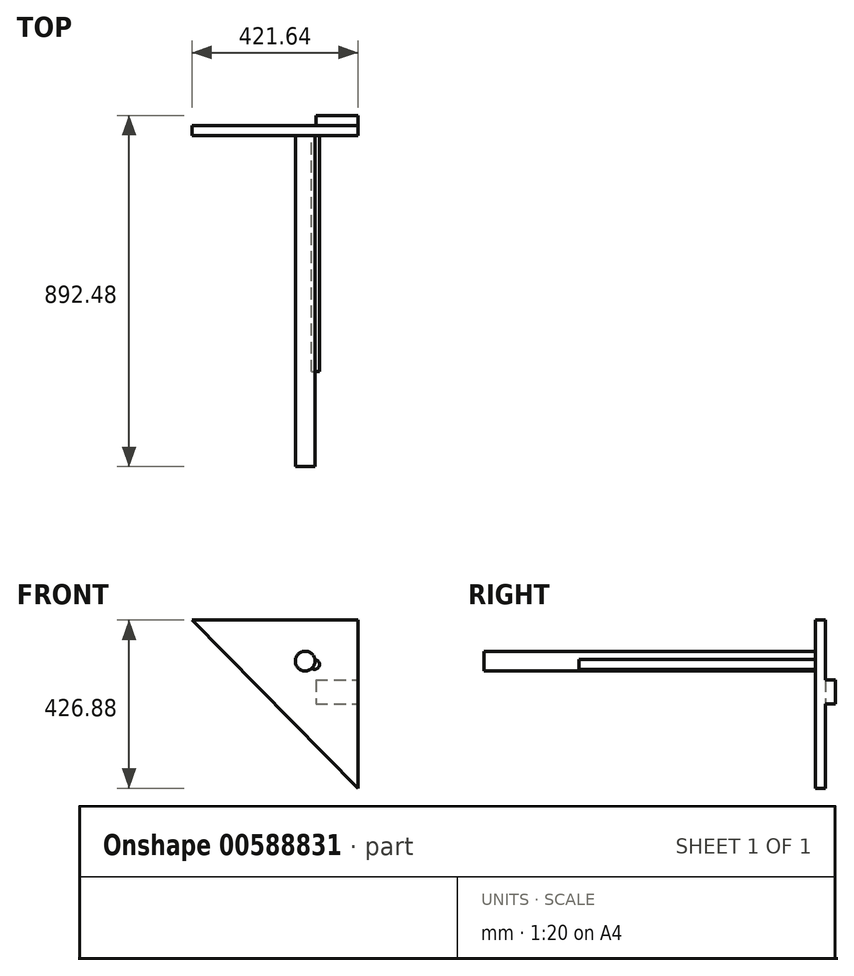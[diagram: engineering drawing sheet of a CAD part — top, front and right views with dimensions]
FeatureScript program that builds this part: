
annotation { "Feature Type Name" : "Feature", "Feature Type Description" : "" }
export const myFeature = defineFeature(function(context is Context, id is Id, definition is map)
    precondition{}
    {
        {
            var Q0;
            Q0=qCreatedBy(makeId("Front.planeOp"),FACE);
            var sketch = newSketch(context, id + "F0", { "sketchPlane" : qUnion([Q0])});
            skLineSegment(sketch, "E0", {"start": v(-421.64, 0) * mm, "end": v(0, 0) * mm});
            skLineSegment(sketch, "E1", {"start": v(0, 0) * mm, "end": v(0, -426.88) * mm});
            skLineSegment(sketch, "E2", {"start": v(0, -426.88) * mm, "end": v(-421.64, 0) * mm});
            skSolve(sketch);
        }
        {
            var Q0;
            Q0 = qSketchRegion(id + "F0", true);
            extrude(context, id + "F1", {"entities" : qUnion([Q0]), "depth" : 25.4 * mm, "offsetDistance" : 25.4 * mm});
        }
        {
            var Q0;
            Q0=makeQuery(id+"F1.opExtrude","CAP_FACE",FACE,{"disambiguationData":[OSD([sQuery(id+"F0.wireOp",EDGE,"E0"),sQuery(id+"F0.wireOp",EDGE,"E1"),sQuery(id+"F0.wireOp",EDGE,"E2")])],"isStart":false});
            var sketch = newSketch(context, id + "F2", { "sketchPlane" : qUnion([Q0])});
            skCircle(sketch, "E3", {"center": v(-110.56, -112.6) * mm, "radius": 12.5 * mm});
            skSolve(sketch);
        }
        {
            var Q0;
            Q0 = qSketchRegion(id + "F2", true);
            extrude(context, id + "F3", {"entities" : qUnion([Q0]), "operationType" : NewBodyOperationType.ADD, "endBound" : BoundingType.THROUGH_ALL, "depth" : 25.4 * mm, "offsetDistance" : 25.4 * mm});
        }
        {
            var Q0;
            Q0=makeQuery(id+"F1.opExtrude","CAP_FACE",FACE,{"disambiguationData":[OSD([sQuery(id+"F0.wireOp",EDGE,"E0"),sQuery(id+"F0.wireOp",EDGE,"E1"),sQuery(id+"F0.wireOp",EDGE,"E2")])],"isStart":true});
            var sketch = newSketch(context, id + "F4", { "sketchPlane" : qUnion([Q0])});
            skCircle(sketch, "E4", {"center": v(134.35, -104.08) * mm, "radius": 25 * mm});
            skSolve(sketch);
        }
        {
            var Q0;
            Q0 = qSketchRegion(id + "F4", true);
            extrude(context, id + "F5", {"entities" : qUnion([Q0]), "operationType" : NewBodyOperationType.ADD, "endBound" : BoundingType.THROUGH_ALL, "oppositeDirection" : true, "depth" : 25.4 * mm, "offsetDistance" : 25.4 * mm});
        }
        {
            var Q0;
            Q0=makeQuery(id+"F1.opExtrude","CAP_FACE",FACE,{"disambiguationData":[OSD([sQuery(id+"F0.wireOp",EDGE,"E0"),sQuery(id+"F0.wireOp",EDGE,"E1"),sQuery(id+"F0.wireOp",EDGE,"E2")])],"isStart":true});
            var sketch = newSketch(context, id + "F6", { "sketchPlane" : qUnion([Q0])});
            skLineSegment(sketch, "E5.bottom", {"start": v(107.16, -152.4) * mm, "end": v(0, -152.4) * mm});
            skLineSegment(sketch, "E5.top", {"start": v(107.16, -213.44) * mm, "end": v(0, -213.44) * mm});
            skLineSegment(sketch, "E5.left", {"start": v(107.16, -152.4) * mm, "end": v(107.16, -213.44) * mm});
            skLineSegment(sketch, "E5.right", {"start": v(0, -152.4) * mm, "end": v(0, -213.44) * mm});
            skSolve(sketch);
        }
        {
            var Q0;
            Q0 = qSketchRegion(id + "F6", true);
            extrude(context, id + "F7", {"entities" : qUnion([Q0]), "operationType" : NewBodyOperationType.ADD, "depth" : 25.4 * mm, "offsetDistance" : 25.4 * mm});
        }
    });
